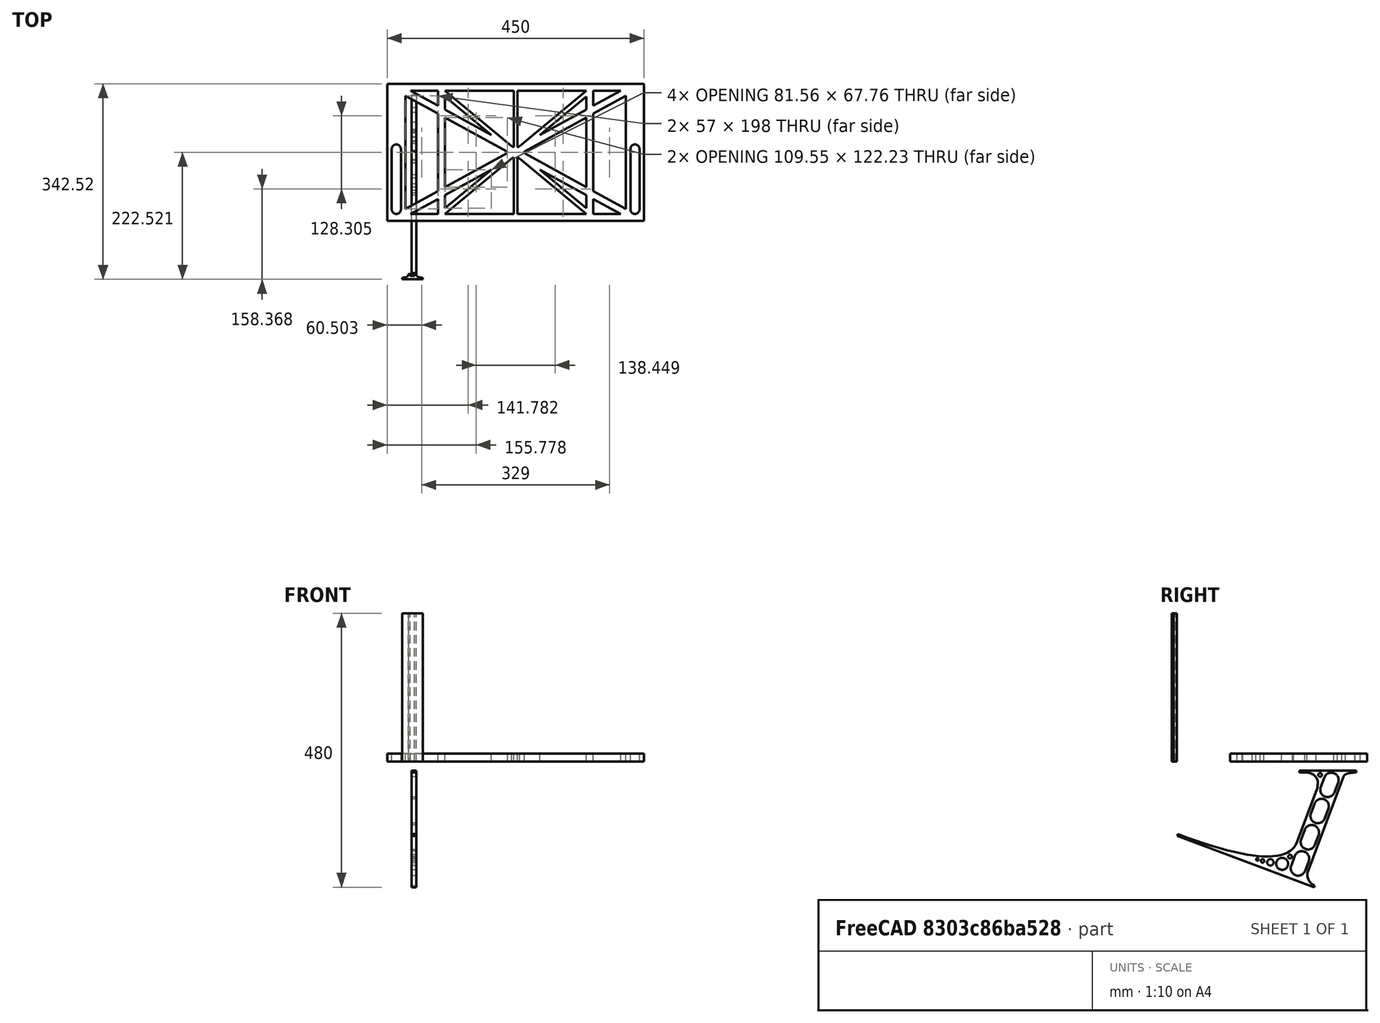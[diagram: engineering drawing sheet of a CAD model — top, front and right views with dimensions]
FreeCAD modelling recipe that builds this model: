
FCSTD DOCUMENT  (FreeCAD 0.19R0.19.2)
Label: laptopStand063
License: All rights reserved
LicenseURL: http://en.wikipedia.org/wiki/All_rights_reserved
objects: Sketcher::SketchObject×3, Part::Extrusion×3
note: 6 computed .brp shape members not serialized (recipe doc carries the construction recipe); baked Part::Feature solids carry a one-line shape summary decoded from their .brp

FEATURE [Sketcher::SketchObject] Sketch
  FullyConstrained = false
  sketch-geometry (102):
    g0: LineSegment StartX=375.073 StartY=115.221 StartZ=0 EndX=318.073 EndY=83.9235 EndZ=0
    g1: LineSegment StartX=-10.9272 StartY=-82.7794 StartZ=0 EndX=46.0728 EndY=-51.4823 EndZ=0
    g2: LineSegment StartX=366.073 StartY=-91.7794 StartZ=0 EndX=318.073 EndY=-65.424 EndZ=0
    g3: LineSegment StartX=-10.9272 StartY=77.3346 StartZ=0 EndX=-10.9272 EndY=-82.7794 EndZ=0
    g4: LineSegment StartX=375.073 StartY=-82.7794 StartZ=0 EndX=375.073 EndY=115.221 EndZ=0
    g5: LineSegment StartX=-1.92719 StartY=-91.7794 StartZ=0 EndX=46.0728 EndY=-91.7794 EndZ=0
    g6: LineSegment StartX=318.073 StartY=124.221 StartZ=0 EndX=366.073 EndY=124.221 EndZ=0
    g7: LineSegment StartX=306.073 StartY=-81.8102 StartZ=0 EndX=224.513 EndY=-14.0532 EndZ=0
    g8: LineSegment StartX=58.0728 StartY=114.251 StartZ=0 EndX=139.632 EndY=46.4944 EndZ=0
    g9: LineSegment StartX=306.073 StartY=124.221 StartZ=0 EndX=189.124 EndY=27.0628 EndZ=0
    g10: LineSegment StartX=58.0728 StartY=-91.7794 StartZ=0 EndX=175.022 EndY=5.37834 EndZ=0
    g11: LineSegment StartX=58.0728 StartY=-81.8102 StartZ=0 EndX=58.0728 EndY=-58.8351 EndZ=0
    g12: LineSegment StartX=318.073 StartY=124.221 StartZ=0 EndX=318.073 EndY=97.8651 EndZ=0
    g13: LineSegment StartX=306.073 StartY=114.251 StartZ=0 EndX=306.073 EndY=91.2763 EndZ=0
    g14: LineSegment StartX=224.513 StartY=46.4944 StartZ=0 EndX=306.073 EndY=114.251 EndZ=0
    g15: LineSegment StartX=175.022 StartY=27.0628 StartZ=0 EndX=58.0728 EndY=124.221 EndZ=0
    g16: LineSegment StartX=139.632 StartY=-14.0532 StartZ=0 EndX=58.0728 EndY=-81.8102 EndZ=0
    g17: LineSegment StartX=224.513 StartY=46.4944 StartZ=0 EndX=306.073 EndY=91.2763 EndZ=0
    g18: LineSegment StartX=139.632 StartY=-14.0532 StartZ=0 EndX=58.0728 EndY=-58.8351 EndZ=0
    g19: LineSegment StartX=189.124 StartY=5.37834 StartZ=0 EndX=306.073 EndY=-91.7794 EndZ=0
    g20: LineSegment StartX=306.073 StartY=77.3346 StartZ=0 EndX=306.073 EndY=-44.8935 EndZ=0
    g21: LineSegment StartX=318.073 StartY=83.9235 StartZ=0 EndX=318.073 EndY=-51.4823 EndZ=0
    g22: LineSegment StartX=318.073 StartY=97.8651 StartZ=0 EndX=366.073 EndY=124.221 EndZ=0
    g23: LineSegment StartX=306.073 StartY=-58.8351 StartZ=0 EndX=224.513 EndY=-14.0532 EndZ=0
    g24: LineSegment StartX=306.073 StartY=-58.8351 StartZ=0 EndX=306.073 EndY=-81.8102 EndZ=0
    g25: LineSegment StartX=318.073 StartY=-51.4823 StartZ=0 EndX=375.073 EndY=-82.7794 EndZ=0
    g26: LineSegment StartX=318.073 StartY=-65.424 StartZ=0 EndX=318.073 EndY=-91.7794 EndZ=0
    g27: LineSegment StartX=318.073 StartY=-91.7794 StartZ=0 EndX=366.073 EndY=-91.7794 EndZ=0
    g28: LineSegment StartX=58.0728 StartY=-44.8935 StartZ=0 EndX=58.0728 EndY=77.3346 EndZ=0
    g29: LineSegment StartX=46.0728 StartY=-65.424 StartZ=0 EndX=-1.92719 EndY=-91.7794 EndZ=0
    g30: LineSegment StartX=46.0728 StartY=-65.424 StartZ=0 EndX=46.0728 EndY=-91.7794 EndZ=0
    g31: LineSegment StartX=58.0728 StartY=91.2763 StartZ=0 EndX=58.0728 EndY=114.251 EndZ=0
    g32: LineSegment StartX=46.0728 StartY=77.3346 StartZ=0 EndX=46.0728 EndY=-51.4823 EndZ=0
    g33: LineSegment StartX=58.0728 StartY=91.2763 StartZ=0 EndX=139.632 EndY=46.4944 EndZ=0
    g34: LineSegment StartX=-42.9272 StartY=136.221 StartZ=0 EndX=-42.9272 EndY=-103.779 EndZ=0
    g35: LineSegment StartX=407.073 StartY=136.221 StartZ=0 EndX=407.073 EndY=-103.779 EndZ=0
    g36: LineSegment StartX=179.022 StartY=27.0628 StartZ=0 EndX=179.022 EndY=124.221 EndZ=0
    g37: LineSegment StartX=185.124 StartY=27.0628 StartZ=0 EndX=185.124 EndY=124.221 EndZ=0
    g38: ArcOfCircle CenterX=-26.9272 CenterY=22.1087 CenterZ=0 NormalX=0 NormalY=0 NormalZ=1 AngleXU=0 Radius=8 StartAngle=1e-16 EndAngle=3.14159
    g39: ArcOfCircle CenterX=-26.9272 CenterY=-83.7794 CenterZ=0 NormalX=0 NormalY=0 NormalZ=1 AngleXU=0 Radius=8 StartAngle=3.14159 EndAngle=6.28319
    g40: LineSegment StartX=-34.9272 StartY=22.1087 StartZ=0 EndX=-34.9272 EndY=-83.7794 EndZ=0
    g41: LineSegment StartX=-18.9272 StartY=22.1087 StartZ=0 EndX=-18.9272 EndY=-83.7794 EndZ=0
    g42: LineSegment StartX=185.124 StartY=-91.7794 StartZ=0 EndX=306.073 EndY=-91.7794 EndZ=0
    g43: LineSegment StartX=179.022 StartY=-91.7794 StartZ=0 EndX=58.0728 EndY=-91.7794 EndZ=0
    g44: LineSegment StartX=306.073 StartY=124.221 StartZ=0 EndX=185.124 EndY=124.221 EndZ=0
    g45: LineSegment StartX=179.022 StartY=124.221 StartZ=0 EndX=58.0728 EndY=124.221 EndZ=0
    g46: ArcOfCircle CenterX=391.073 CenterY=22.1087 CenterZ=0 NormalX=0 NormalY=0 NormalZ=1 AngleXU=0 Radius=8 StartAngle=-4.4e-15 EndAngle=3.14159
    g47: LineSegment StartX=399.073 StartY=22.1087 StartZ=0 EndX=399.073 EndY=-83.7794 EndZ=0
    g48: LineSegment StartX=383.073 StartY=22.1087 StartZ=0 EndX=383.073 EndY=-83.7794 EndZ=0
    g49: ArcOfCircle CenterX=391.073 CenterY=-83.7794 CenterZ=0 NormalX=0 NormalY=0 NormalZ=1 AngleXU=0 Radius=8 StartAngle=3.14159 EndAngle=6.28319
    g50: Circle CenterX=175.022 CenterY=27.0628 CenterZ=0 NormalX=0 NormalY=0 NormalZ=1 AngleXU=0 Radius=1
    g51: Circle CenterX=179.022 CenterY=24.8665 CenterZ=0 NormalX=0 NormalY=0 NormalZ=1 AngleXU=0 Radius=1
    g52: Circle CenterX=179.022 CenterY=27.0628 CenterZ=0 NormalX=0 NormalY=0 NormalZ=1 AngleXU=0 Radius=1
    g53: BSplineCurve PolesCount=3 KnotsCount=2 Degree=2 IsPeriodic=0
    g54: GeomPoint X=175.022 Y=27.0628 Z=0
    g55: GeomPoint X=179.022 Y=27.0628 Z=0
    g56: Circle CenterX=189.124 CenterY=27.0628 CenterZ=0 NormalX=0 NormalY=0 NormalZ=1 AngleXU=0 Radius=1
    g57: Circle CenterX=185.124 CenterY=24.8665 CenterZ=0 NormalX=0 NormalY=0 NormalZ=1 AngleXU=0 Radius=1
    g58: Circle CenterX=185.124 CenterY=27.0628 CenterZ=0 NormalX=0 NormalY=0 NormalZ=1 AngleXU=0 Radius=1
    g59: BSplineCurve PolesCount=3 KnotsCount=2 Degree=2 IsPeriodic=0
    g60: GeomPoint X=189.124 Y=27.0628 Z=0
    g61: GeomPoint X=185.124 Y=27.0628 Z=0
    g62: Circle CenterX=175.022 CenterY=5.37834 CenterZ=0 NormalX=0 NormalY=0 NormalZ=1 AngleXU=0 Radius=1
    g63: Circle CenterX=179.022 CenterY=7.57463 CenterZ=0 NormalX=0 NormalY=0 NormalZ=1 AngleXU=0 Radius=1
    g64: Circle CenterX=179.022 CenterY=5.34704 CenterZ=0 NormalX=0 NormalY=0 NormalZ=1 AngleXU=0 Radius=1
    g65: BSplineCurve PolesCount=3 KnotsCount=2 Degree=2 IsPeriodic=0
    g66: GeomPoint X=175.022 Y=5.37834 Z=0
    g67: GeomPoint X=179.022 Y=5.34704 Z=0
    g68: Circle CenterX=189.124 CenterY=5.37834 CenterZ=0 NormalX=0 NormalY=0 NormalZ=1 AngleXU=0 Radius=1
    g69: Circle CenterX=185.124 CenterY=7.57463 CenterZ=0 NormalX=0 NormalY=0 NormalZ=1 AngleXU=0 Radius=1
    g70: Circle CenterX=185.124 CenterY=5.34704 CenterZ=0 NormalX=0 NormalY=0 NormalZ=1 AngleXU=0 Radius=1
    g71: BSplineCurve PolesCount=3 KnotsCount=2 Degree=2 IsPeriodic=0
    g72: GeomPoint X=189.124 Y=5.37834 Z=0
    g73: GeomPoint X=185.124 Y=5.34704 Z=0
    g74: LineSegment StartX=179.022 StartY=5.34704 StartZ=0 EndX=179.022 EndY=-91.7794 EndZ=0
    g75: LineSegment StartX=185.124 StartY=-91.7794 StartZ=0 EndX=185.124 EndY=5.34704 EndZ=0
    g76: Circle CenterX=165.871 CenterY=18.1458 CenterZ=0 NormalX=0 NormalY=0 NormalZ=1 AngleXU=0 Radius=1
    g77: Circle CenterX=169.377 CenterY=16.2206 CenterZ=0 NormalX=0 NormalY=0 NormalZ=1 AngleXU=0 Radius=1
    g78: Circle CenterX=165.871 CenterY=14.2954 CenterZ=0 NormalX=0 NormalY=0 NormalZ=1 AngleXU=0 Radius=1
    g79: BSplineCurve PolesCount=3 KnotsCount=2 Degree=2 IsPeriodic=0
    g80: GeomPoint X=165.871 Y=18.1458 Z=0
    g81: GeomPoint X=165.871 Y=14.2954 Z=0
    g82: Circle CenterX=198.275 CenterY=18.1458 CenterZ=0 NormalX=0 NormalY=0 NormalZ=1 AngleXU=0 Radius=1
    g83: Circle CenterX=194.768 CenterY=16.2206 CenterZ=0 NormalX=0 NormalY=0 NormalZ=1 AngleXU=0 Radius=1
    g84: Circle CenterX=198.275 CenterY=14.2954 CenterZ=0 NormalX=0 NormalY=0 NormalZ=1 AngleXU=0 Radius=1
    g85: BSplineCurve PolesCount=3 KnotsCount=2 Degree=2 IsPeriodic=0
    g86: GeomPoint X=198.275 Y=18.1458 Z=0
    g87: GeomPoint X=198.275 Y=14.2954 Z=0
    g88: LineSegment StartX=165.871 StartY=18.1458 StartZ=0 EndX=58.0728 EndY=77.3346 EndZ=0
    g89: LineSegment StartX=58.0728 StartY=-44.8935 StartZ=0 EndX=165.871 EndY=14.2954 EndZ=0
    g90: LineSegment StartX=198.275 StartY=18.1458 StartZ=0 EndX=306.073 EndY=77.3346 EndZ=0
    g91: LineSegment StartX=198.275 StartY=14.2954 StartZ=0 EndX=306.073 EndY=-44.8935 EndZ=0
    g92: LineSegment StartX=407.073 StartY=-103.779 StartZ=0 EndX=-42.9272 EndY=-103.779 EndZ=0
    g93: LineSegment StartX=407.073 StartY=136.221 StartZ=0 EndX=-42.9272 EndY=136.221 EndZ=0
    g94: LineSegment StartX=-26.9272 StartY=136.221 StartZ=0 EndX=-26.9272 EndY=98.2206 EndZ=0
    g95: LineSegment StartX=46.0728 StartY=77.3346 StartZ=0 EndX=-10.9272 EndY=77.3346 EndZ=0
    g96: LineSegment StartX=46.0728 StartY=105.865 StartZ=0 EndX=31.5028 EndY=105.865 EndZ=0
    g97: LineSegment StartX=46.0728 StartY=124.221 StartZ=0 EndX=46.0728 EndY=105.865 EndZ=0
    g98: LineSegment StartX=-1.92719 StartY=124.221 StartZ=0 EndX=31.5028 EndY=105.865 EndZ=0
    g99: LineSegment StartX=46.0728 StartY=124.221 StartZ=0 EndX=-1.92719 EndY=124.221 EndZ=0
    g100: LineSegment StartX=318.073 StartY=83.9235 StartZ=0 EndX=375.073 EndY=83.9235 EndZ=0
    g101: LineSegment StartX=318.073 StartY=97.8651 StartZ=0 EndX=318.073 EndY=105.865 EndZ=0
  constraints (191):
    c: Horizontal(g5)
    c: Horizontal(g6)
    c: Coincident(g33,g8)
    c: Coincident(g14,g17)
    c: Coincident(g18,g16)
    c: Coincident(g23,g7)
    c: Coincident(g14,g13)
    c: Tangent(g13,g20)
    c: Tangent(g12,g21)
    c: Coincident(g17,g13)
    c: Tangent(g17,g22)
    c: Coincident(g0,g21)
    c: Coincident(g24,g7)
    c: Tangent(g2,g23)
    c: Tangent(g20,g24)
    c: Coincident(g21,g25)
    c: Coincident(g26,g2)
    c: Tangent(g21,g26)
    c: Coincident(g16,g11)
    c: Tangent(g11,g28)
    c: Coincident(g18,g11)
    c: Tangent(g18,g29)
    c: Coincident(g30,g29)
    c: Coincident(g1,g32)
    c: Tangent(g28,g31)
    c: Coincident(g8,g31)
    c: Coincident(g33,g31)
    c: Block(g15)
    c: Block(g9)
    c: Block(g12)
    c: Block(g22)
    c: Block(g0)
    c: Block(g25)
    c: Block(g4)
    c: Block(g23)
    c: Block(g24)
    c: Block(g2)
    c: Block(g26)
    c: Block(g14)
    c: Block(g19)
    c: Block(g10)
    c: Block(g18)
    c: Block(g16)
    c: Block(g30)
    c: Block(g29)
    c: Block(g1)
    c: Block(g3)
    c: Block(g8)
    c: Block(g31)
    c: Block(g20)
    c: Block(g6)
    c: Block(g27)
    c: Block(g5)
    c: Vertical(g34)
    c: Vertical(g35)
    c: Block(g35)
    c: Block(g34)
    c: Vertical(g36)
    c: Vertical(g37)
    c: Block(g36)
    c: Block(g37)
    c: Tangent(g38,g41) = 1.5708
    c: Tangent(g38,g40) = -1.5708
    c: Tangent(g40,g39) = -1.5708
    c: Tangent(g41,g39) = 1.5708
    c: Vertical(g40)
    c: Equal(g38,g39)
    c: Block(g41)
    c: Block(g40)
    c: Coincident(g42,g19)
    c: Horizontal(g42)
    c: Coincident(g43,g10)
    c: Horizontal(g43)
    c: Coincident(g44,g9)
    c: Coincident(g44,g37)
    c: Horizontal(g44)
    c: Coincident(g45,g36)
    c: Coincident(g45,g15)
    c: Horizontal(g45)
    c: Tangent(g46,g47) = 1.5708
    c: Tangent(g47,g49) = 1.5708
    c: Equal(g46,g49)
    c: Coincident(g48,g46)
    c: Coincident(g48,g49)
    c: Block(g47)
    c: Block(g48)
    c: Coincident(g53,g15)
    c: Weight(g50) = 1
    c: Equal(g50,g51)
    c: Equal(g50,g52)
    c: Coincident(g53,g36)
    c: InternalAlignment(g50,g53)
    c: InternalAlignment(g51,g53)
    c: InternalAlignment(g52,g53)
    c: InternalAlignment(g54,g53)
    c: InternalAlignment(g55,g53)
    c: Coincident(g59,g9)
    c: Weight(g56) = 1
    c: Equal(g56,g57)
    c: Equal(g56,g58)
    c: Coincident(g59,g37)
    c: InternalAlignment(g56,g59)
    c: InternalAlignment(g57,g59)
    c: InternalAlignment(g58,g59)
    c: InternalAlignment(g60,g59)
    c: InternalAlignment(g61,g59)
    c: Block(g59)
    c: Block(g53)
    c: Coincident(g65,g10)
    c: Weight(g62) = 1
    c: Equal(g62,g63)
    c: Equal(g62,g64)
    c: InternalAlignment(g62,g65)
    c: InternalAlignment(g63,g65)
    c: InternalAlignment(g64,g65)
    c: InternalAlignment(g66,g65)
    c: InternalAlignment(g67,g65)
    c: Weight(g68) = 1
    c: Equal(g68,g69)
    c: Equal(g68,g70)
    c: InternalAlignment(g68,g71)
    c: InternalAlignment(g69,g71)
    c: InternalAlignment(g70,g71)
    c: InternalAlignment(g72,g71)
    c: InternalAlignment(g73,g71)
    c: Block(g71)
    c: Block(g65)
    c: Coincident(g74,g65)
    c: Coincident(g74,g43)
    c: Vertical(g74)
    c: Coincident(g75,g42)
    c: Coincident(g75,g71)
    c: Vertical(g75)
    c: Weight(g76) = 1
    c: Equal(g76,g77)
    c: Equal(g76,g78)
    c: InternalAlignment(g76,g79)
    c: InternalAlignment(g77,g79)
    c: InternalAlignment(g78,g79)
    c: InternalAlignment(g80,g79)
    c: InternalAlignment(g81,g79)
    c: Weight(g82) = 1
    c: Equal(g82,g83)
    c: Equal(g82,g84)
    c: InternalAlignment(g82,g85)
    c: InternalAlignment(g83,g85)
    c: InternalAlignment(g84,g85)
    c: InternalAlignment(g86,g85)
    c: InternalAlignment(g87,g85)
    c: Block(g79)
    c: Block(g85)
    c: Coincident(g88,g79)
    c: Coincident(g88,g28)
    c: Coincident(g89,g28)
    c: Coincident(g89,g79)
    c: Coincident(g90,g85)
    c: Coincident(g90,g20)
    c: Coincident(g91,g85)
    c: Coincident(g91,g20)
    c: Block(g28)
    c: Coincident(g92,g35)
    c: Coincident(g92,g34)
    c: Horizontal(g92)
    c: Distance(g92) = 450
    c: Coincident(g93,g35)
    c: Coincident(g93,g34)
    c: Horizontal(g93)
    c: PointOnObject(g94,g93)
    c: Vertical(g94)
    c: Distance(g94) = 38
    c: Horizontal(g95)
    c: Coincident(g32,g95)
    c: Horizontal(g96)
    c: Vertical(g97)
    c: Block(g97)
    c: Block(g96)
    c: Block(g95)
    c: Distance(g97) = 18.3554
    c: Coincident(g99,g97)
    c: Coincident(g99,g98)
    c: Horizontal(g99)
    c: Block(g99)
    c: Block(g98)
    c: Coincident(g96,g98)
    c: Coincident(g3,g95)
    c: Coincident(g100,g0)
    c: Horizontal(g100)
    c: Vertical(g101)
    c: Distance(g101) = 8
    c: Coincident(g101,g12)
    c: PointOnObject(g100,g4)
FEATURE [Sketcher::SketchObject] Sketch001
  FullyConstrained = true
  MapMode = 4
  Placement = pos=(0,0,0) rot=(0.57735,0.57735,0.57735;2.0944rad)
  Support = -> [Sketch]
  sketch-geometry (46):
    g0: BSplineCurve PolesCount=3 KnotsCount=2 Degree=2 IsPeriodic=0
    g1: ArcOfCircle CenterX=73.1223 CenterY=-32.291 CenterZ=0 NormalX=0 NormalY=0 NormalZ=1 AngleXU=0 Radius=13 StartAngle=5.92268 EndAngle=9.06428
    g2: ArcOfCircle CenterX=66.7816 CenterY=-49.1439 CenterZ=0 NormalX=0 NormalY=0 NormalZ=1 AngleXU=0 Radius=13 StartAngle=2.78068 EndAngle=5.92131
    g3: ArcOfCircle CenterX=55.9263 CenterY=-78.1807 CenterZ=0 NormalX=0 NormalY=0 NormalZ=1 AngleXU=0 Radius=13 StartAngle=5.92268 EndAngle=9.06428
    g4: ArcOfCircle CenterX=49.5884 CenterY=-95.0342 CenterZ=0 NormalX=0 NormalY=0 NormalZ=1 AngleXU=0 Radius=13 StartAngle=2.78068 EndAngle=5.92131
    g5: ArcOfCircle CenterX=38.7206 CenterY=-124.067 CenterZ=0 NormalX=0 NormalY=0 NormalZ=1 AngleXU=0 Radius=13 StartAngle=5.92268 EndAngle=9.06428
    g6: ArcOfCircle CenterX=32.3875 CenterY=-140.92 CenterZ=0 NormalX=0 NormalY=0 NormalZ=1 AngleXU=0 Radius=13 StartAngle=2.78068 EndAngle=5.92131
    g7: ArcOfCircle CenterX=21.4715 CenterY=-169.934 CenterZ=0 NormalX=0 NormalY=0 NormalZ=1 AngleXU=0 Radius=13 StartAngle=5.92268 EndAngle=9.06428
    g8: ArcOfCircle CenterX=15.1336 CenterY=-186.787 CenterZ=0 NormalX=0 NormalY=0 NormalZ=1 AngleXU=0 Radius=13 StartAngle=2.78068 EndAngle=5.92131
    g9-g12: Circle x4 (B-spline internal-alignment scaffolding for g13; pole/knot coordinates omitted)
    g13: BSplineCurve PolesCount=4 KnotsCount=2 Degree=3 IsPeriodic=0
    g14: GeomPoint X=28.8094 Y=-19.0875 Z=0
    g15: GeomPoint X=47.0443 Y=-50.4712 Z=0
    g16: Circle CenterX=53.5586 CenterY=-23.2695 CenterZ=0 NormalX=0 NormalY=0 NormalZ=1 AngleXU=0 Radius=3.24518
    g17: Circle CenterX=-195.441 CenterY=-127.082 CenterZ=0 NormalX=0 NormalY=0 NormalZ=1 AngleXU=0 Radius=1
    g18: Circle CenterX=-8.24091 CenterY=-197.481 CenterZ=0 NormalX=0 NormalY=0 NormalZ=1 AngleXU=0 Radius=1
    g19: Circle CenterX=12.8789 CenterY=-141.321 CenterZ=0 NormalX=0 NormalY=0 NormalZ=1 AngleXU=0 Radius=1
    g20: BSplineCurve PolesCount=3 KnotsCount=2 Degree=2 IsPeriodic=0
    g21: GeomPoint X=-195.441 Y=-127.082 Z=0
    g22: GeomPoint X=12.8789 Y=-141.321 Z=0
    g23: Circle CenterX=-12.8016 CenterY=-179.036 CenterZ=0 NormalX=0 NormalY=0 NormalZ=1 AngleXU=0 Radius=10.5072
    g24: Circle CenterX=0.933922 CenterY=-166.43 CenterZ=0 NormalX=0 NormalY=0 NormalZ=1 AngleXU=0 Radius=3.26661
    g25: Circle CenterX=-33.5518 CenterY=-176.44 CenterZ=0 NormalX=0 NormalY=0 NormalZ=1 AngleXU=0 Radius=5.64388
    g26: Circle CenterX=-47.2366 CenterY=-173.859 CenterZ=0 NormalX=0 NormalY=0 NormalZ=1 AngleXU=0 Radius=3.01653
    g27: Circle CenterX=-56.2595 CenterY=-171.456 CenterZ=0 NormalX=0 NormalY=0 NormalZ=1 AngleXU=0 Radius=2.12826
    g28: ArcOfCircle CenterX=51.2151 CenterY=-198.473 CenterZ=0 NormalX=0 NormalY=0 NormalZ=1 AngleXU=0 Radius=20 StartAngle=2.78189 EndAngle=4.35269
    g29: LineSegment StartX=32.4951 StartY=-191.433 StartZ=0 EndX=94.6578 EndY=-26.1352 EndZ=0
    g30: LineSegment StartX=43.1192 StartY=-220.001 StartZ=0 EndX=-196.497 EndY=-129.89 EndZ=0
    g31: LineSegment StartX=43.1192 StartY=-220.001 StartZ=0 EndX=44.1752 EndY=-217.193 EndZ=0
    g32: LineSegment StartX=117.223 StartY=-19.0875 StartZ=0 EndX=117.223 EndY=-16.0875 EndZ=0
    g33: LineSegment StartX=117.223 StartY=-16.0875 StartZ=0 EndX=17.2232 EndY=-16.0875 EndZ=0
    g34: LineSegment StartX=17.2232 StartY=-16.0875 StartZ=0 EndX=17.2232 EndY=-19.0875 EndZ=0
    g35: LineSegment StartX=28.8094 StartY=-19.0875 StartZ=0 EndX=17.2232 EndY=-19.0875 EndZ=0
    g36: LineSegment StartX=47.0443 StartY=-50.4712 StartZ=0 EndX=12.8789 EndY=-141.321 EndZ=0
    g37: LineSegment StartX=-195.441 StartY=-127.082 StartZ=0 EndX=-196.497 EndY=-129.89 EndZ=0
    g38: LineSegment StartX=85.2866 StartY=-36.8766 StartZ=0 EndX=78.9396 EndY=-53.7463 EndZ=0
    g39: LineSegment StartX=60.9579 StartY=-27.7053 StartZ=0 EndX=54.6191 EndY=-44.5532 EndZ=0
    g40: LineSegment StartX=68.0907 StartY=-82.7664 StartZ=0 EndX=61.7465 EndY=-99.6365 EndZ=0
    g41: LineSegment StartX=43.7619 StartY=-73.595 StartZ=0 EndX=37.426 EndY=-90.4435 EndZ=0
    g42: LineSegment StartX=50.885 StartY=-128.652 StartZ=0 EndX=44.5456 EndY=-145.522 EndZ=0
    g43: LineSegment StartX=26.5562 StartY=-119.481 StartZ=0 EndX=20.2251 EndY=-136.329 EndZ=0
    g44: LineSegment StartX=9.3071 StartY=-165.349 StartZ=0 EndX=2.97115 EndY=-182.197 EndZ=0
    g45: LineSegment StartX=33.6358 StartY=-174.52 StartZ=0 EndX=27.2917 EndY=-191.39 EndZ=0
  constraints (71):
    c: Block(g0)
    c: Block(g1)
    c: Block(g2)
    c: Block(g4)
    c: Block(g3)
    c: Block(g6)
    c: Block(g5)
    c: Block(g8)
    c: Block(g7)
    c: Weight(g9) = 1
    c: Equal(g9,g10)
    c: Equal(g9,g11)
    c: Equal(g9,g12)
    c: InternalAlignment(g9-g12 -> g13) x4
    c: InternalAlignment(g14,g13)
    c: InternalAlignment(g15,g13)
    c: Block(g16)
    c: Weight(g17) = 1
    c: Equal(g17,g18)
    c: Equal(g17,g19)
    c: InternalAlignment(g17,g20)
    c: InternalAlignment(g18,g20)
    c: InternalAlignment(g19,g20)
    c: InternalAlignment(g21,g20)
    c: InternalAlignment(g22,g20)
    c: Block(g20)
    c: Block(g23)
    c: Block(g24)
    c: Block(g25)
    c: Block(g26)
    c: Block(g27)
    c: Block(g28)
    c: Coincident(g29,g28)
    c: Coincident(g29,g0)
    c: Block(g13)
    c: Coincident(g31,g30)
    c: Coincident(g31,g28)
    c: Block(g31)
    c: Coincident(g32,g0)
    c: Vertical(g32)
    c: Coincident(g33,g32)
    c: Horizontal(g33)
    c: Coincident(g34,g33)
    c: Vertical(g34)
    c: Block(g33)
    c: Coincident(g35,g13)
    c: Coincident(g35,g34)
    c: Horizontal(g35)
    c: Coincident(g36,g13)
    c: Coincident(g36,g20)
    c: Coincident(g37,g20)
    c: Coincident(g37,g30)
    c: Block(g30)
    c: Coincident(g38,g1)
    c: Coincident(g38,g2)
    c: Coincident(g39,g1)
    c: Coincident(g39,g2)
    c: Coincident(g40,g3)
    c: Coincident(g40,g4)
    c: Coincident(g41,g3)
    c: Coincident(g41,g4)
    c: Coincident(g42,g5)
    c: Coincident(g42,g6)
    c: Coincident(g43,g5)
    c: Coincident(g43,g6)
    c: Coincident(g44,g7)
    c: Coincident(g44,g8)
    c: Coincident(g45,g7)
    c: Coincident(g45,g8)
    c: Distance(g30) = 256
    c: Distance(g33) = 100
FEATURE [Part::Extrusion] Extrude002
  Base = -> Sketch001
  Dir = (1,0,0)
  DirMode = 2
  FaceMakerClass = Part::FaceMakerBullseye
  LengthFwd = 8
  LengthRev = 0
  Solid = true
  Symmetric = false
FEATURE [Sketcher::SketchObject] Sketch002
  FullyConstrained = true
  sketch-geometry (20):
    g0: LineSegment StartX=-2.77179 StartY=-200.304 StartZ=0 EndX=5.22821 EndY=-200.304 EndZ=0
    g1: LineSegment StartX=5.22821 StartY=-200.304 StartZ=0 EndX=5.22821 EndY=-197.304 EndZ=0
    g2: LineSegment StartX=-2.77179 StartY=-200.304 StartZ=0 EndX=-2.77179 EndY=-197.304 EndZ=0
    g3: LineSegment StartX=5.22821 StartY=-197.304 StartZ=0 EndX=8.22821 EndY=-197.304 EndZ=0
    g4: LineSegment StartX=-2.77179 StartY=-197.304 StartZ=0 EndX=-5.77179 EndY=-197.304 EndZ=0
    g5: LineSegment StartX=19.2282 StartY=-203.304 StartZ=0 EndX=19.2282 EndY=-206.304 EndZ=0
    g6: LineSegment StartX=-16.7718 StartY=-203.304 StartZ=0 EndX=-16.7718 EndY=-206.304 EndZ=0
    g7: LineSegment StartX=-16.7718 StartY=-206.304 StartZ=0 EndX=19.2282 EndY=-206.304 EndZ=0
    g8: Circle CenterX=-16.7718 CenterY=-203.304 CenterZ=0 NormalX=0 NormalY=0 NormalZ=1 AngleXU=0 Radius=1
    g9: Circle CenterX=-5.77179 CenterY=-203.304 CenterZ=0 NormalX=0 NormalY=0 NormalZ=1 AngleXU=0 Radius=1
    g10: Circle CenterX=-5.77179 CenterY=-197.304 CenterZ=0 NormalX=0 NormalY=0 NormalZ=1 AngleXU=0 Radius=1
    g11: BSplineCurve PolesCount=3 KnotsCount=2 Degree=2 IsPeriodic=0
    g12: GeomPoint X=-16.7718 Y=-203.304 Z=0
    g13: GeomPoint X=-5.77179 Y=-197.304 Z=0
    g14: Circle CenterX=19.2282 CenterY=-203.304 CenterZ=0 NormalX=0 NormalY=0 NormalZ=1 AngleXU=0 Radius=1
    g15: Circle CenterX=8.22821 CenterY=-203.304 CenterZ=0 NormalX=0 NormalY=0 NormalZ=1 AngleXU=0 Radius=1
    g16: Circle CenterX=8.22821 CenterY=-197.304 CenterZ=0 NormalX=0 NormalY=0 NormalZ=1 AngleXU=0 Radius=1
    g17: BSplineCurve PolesCount=3 KnotsCount=2 Degree=2 IsPeriodic=0
    g18: GeomPoint X=19.2282 Y=-203.304 Z=0
    g19: GeomPoint X=8.22821 Y=-197.304 Z=0
  constraints (41):
    c: Horizontal(g0)
    c: Distance(g0) = 8
    c: Coincident(g1,g0)
    c: Vertical(g1)
    c: Distance(g1) = 3
    c: Coincident(g2,g0)
    c: Vertical(g2)
    c: Distance(g2) = 3
    c: Coincident(g3,g1)
    c: Horizontal(g3)
    c: Distance(g3) = 3
    c: Coincident(g4,g2)
    c: Horizontal(g4)
    c: Distance(g4) = 3
    c: Vertical(g5)
    c: Vertical(g6)
    c: Coincident(g7,g6)
    c: Coincident(g7,g5)
    c: Weight(g8) = 1
    c: Equal(g8,g9)
    c: Equal(g8,g10)
    c: Coincident(g11,g4)
    c: InternalAlignment(g8,g11)
    c: InternalAlignment(g9,g11)
    c: InternalAlignment(g10,g11)
    c: InternalAlignment(g12,g11)
    c: InternalAlignment(g13,g11)
    c: Coincident(g17,g5)
    c: Weight(g14) = 1
    c: Equal(g14,g15)
    c: Equal(g14,g16)
    c: Coincident(g17,g3)
    c: InternalAlignment(g14,g17)
    c: InternalAlignment(g15,g17)
    c: InternalAlignment(g16,g17)
    c: InternalAlignment(g18,g17)
    c: InternalAlignment(g19,g17)
    c: Block(g7)
    c: Block(g17)
    c: Block(g11)
    c: Block(g6)
FEATURE [Part::Extrusion] Extrude003
  Base = -> Sketch002
  Dir = (0,0,1)
  DirMode = 2
  FaceMakerClass = Part::FaceMakerBullseye
  LengthFwd = 260
  LengthRev = 0
  Solid = true
  Symmetric = false
FEATURE [Part::Extrusion] Extrude
  Base = -> Sketch
  Dir = (0,0,1)
  DirMode = 2
  FaceMakerClass = Part::FaceMakerBullseye
  LengthFwd = 14
  LengthRev = 0
  Solid = true
  Symmetric = false
